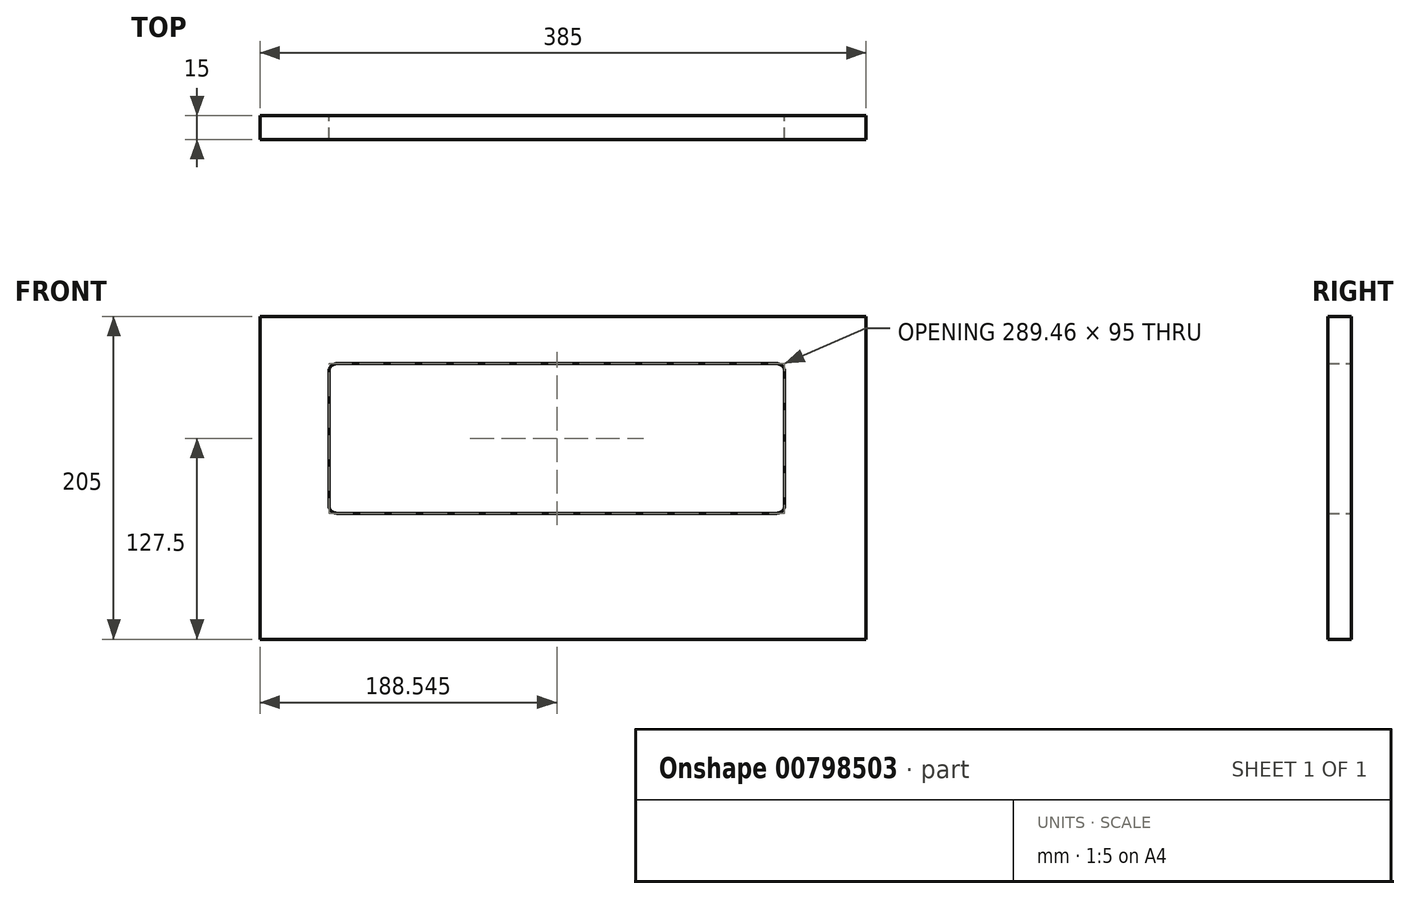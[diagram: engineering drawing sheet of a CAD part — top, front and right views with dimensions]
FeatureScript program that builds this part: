
annotation { "Feature Type Name" : "Feature", "Feature Type Description" : "" }
export const myFeature = defineFeature(function(context is Context, id is Id, definition is map)
    precondition{}
    {
        {
            var Q0;
            Q0=qCreatedBy(makeId("Front.planeOp"),FACE);
            var sketch = newSketch(context, id + "F0", { "sketchPlane" : qUnion([Q0])});
            skLineSegment(sketch, "E0.bottom", {"start": v(0, 0) * mm, "end": v(385, 0) * mm});
            skLineSegment(sketch, "E0.top", {"start": v(0, -205) * mm, "end": v(385, -205) * mm});
            skLineSegment(sketch, "E0.left", {"start": v(0, 0) * mm, "end": v(0, -205) * mm});
            skLineSegment(sketch, "E0.right", {"start": v(385, 0) * mm, "end": v(385, -205) * mm});
            skLineSegment(sketch, "E1.bottom", {"start": v(48.82, -30) * mm, "end": v(328.27, -30) * mm});
            skLineSegment(sketch, "E1.top", {"start": v(48.82, -125) * mm, "end": v(328.27, -125) * mm});
            skLineSegment(sketch, "E1.left", {"start": v(43.82, -35) * mm, "end": v(43.82, -120) * mm});
            skLineSegment(sketch, "E1.right", {"start": v(333.27, -35) * mm, "end": v(333.27, -120) * mm});
            skPoint(sketch, "E2.visualSharp", {"position": v(43.82, -30) * mm});
            skArc(sketch, "E2.filletArc", {"start": v(48.82, -30) * mm, "mid": v(45.28, -31.46) * mm, "end": v(43.82, -35) * mm});
            skPoint(sketch, "E3.visualSharp", {"position": v(43.82, -125) * mm});
            skArc(sketch, "E3.filletArc", {"start": v(43.82, -120) * mm, "mid": v(45.28, -123.54) * mm, "end": v(48.82, -125) * mm});
            skPoint(sketch, "E4.visualSharp", {"position": v(333.27, -125) * mm});
            skArc(sketch, "E4.filletArc", {"start": v(328.27, -125) * mm, "mid": v(331.8, -123.54) * mm, "end": v(333.27, -120) * mm});
            skPoint(sketch, "E5.visualSharp", {"position": v(333.27, -30) * mm});
            skArc(sketch, "E5.filletArc", {"start": v(333.27, -35) * mm, "mid": v(331.8, -31.46) * mm, "end": v(328.27, -30) * mm});
            skSolve(sketch);
        }
        {
            var Q0;
            Q0=makeQuery(id+"F0.imprint","IMPRINT",FACE,{"disambiguationData":[TD([[makeQuery(id+"F0.imprint","IMPRINT",EDGE,{"derivedFrom":sQuery(id+"F0.wireOp",EDGE,"E0.bottom")}),-1.0]])]});
            extrude(context, id + "F1", {"entities" : qUnion([Q0]), "depth" : 15 * mm, "offsetDistance" : 25 * mm});
        }
    });
